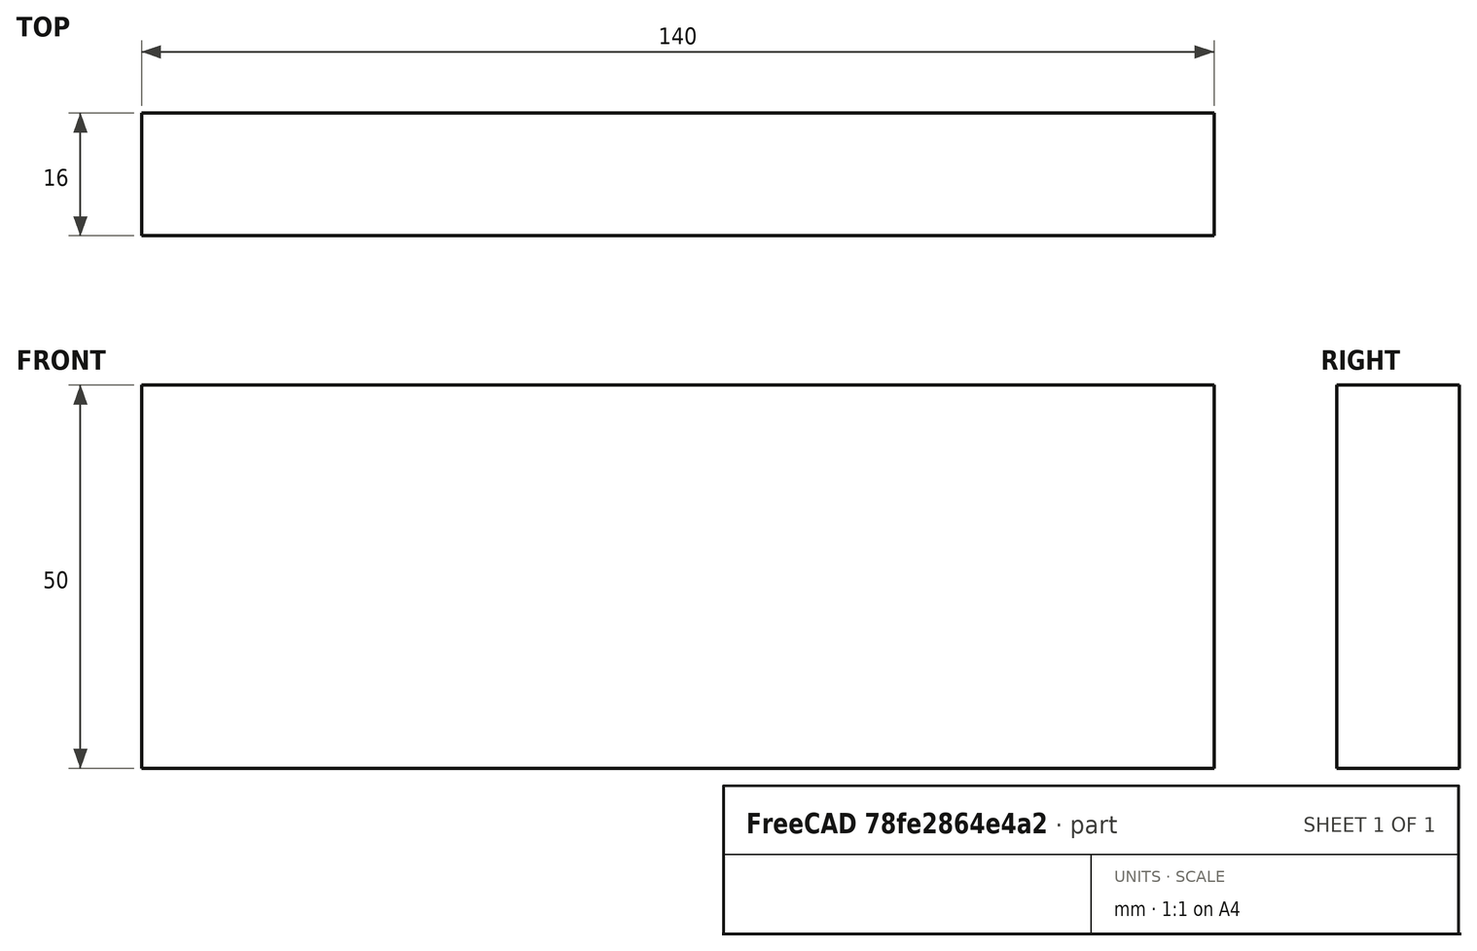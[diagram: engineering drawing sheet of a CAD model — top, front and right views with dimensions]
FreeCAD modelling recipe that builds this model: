
FCSTD DOCUMENT  (FreeCAD 0.15R4671 (Git))
Label: Flat Bar 140x16 EN10058 S235JR
License: All rights reserved
LicenseURL: http://en.wikipedia.org/wiki/All_rights_reserved
objects: Sketcher::SketchObject×1, Part::Extrusion×1
note: 2 computed .brp shape members not serialized (recipe doc carries the construction recipe); baked Part::Feature solids carry a one-line shape summary decoded from their .brp

FEATURE [Sketcher::SketchObject] Sketch
  sketch-geometry (4):
    g0: LineSegment StartX=-70 StartY=-8 StartZ=0 EndX=70 EndY=-8 EndZ=0
    g1: LineSegment StartX=70 StartY=-8 StartZ=0 EndX=70 EndY=8 EndZ=0
    g2: LineSegment StartX=70 StartY=8 StartZ=0 EndX=-70 EndY=8 EndZ=0
    g3: LineSegment StartX=-70 StartY=8 StartZ=0 EndX=-70 EndY=-8 EndZ=0
  constraints (12):
    c: Coincident(g0,g1)
    c: Coincident(g1,g2)
    c: Coincident(g2,g3)
    c: Coincident(g3,g0)
    c: Horizontal(g0)
    c: Horizontal(g2)
    c: Vertical(g1)
    c: Vertical(g3)
    c: Symmetric(g1,g2,g-2)
    c: Symmetric(g0,g1,g-1)
    c: DistanceY(g1) = 16
    c: DistanceX(g0) = 140
FEATURE [Part::Extrusion] Extrude  label="Flat Bar 140x16 EN10058 S235JR"
  Base = -> Sketch
  Dir = (0,0,50)
  Solid = true
